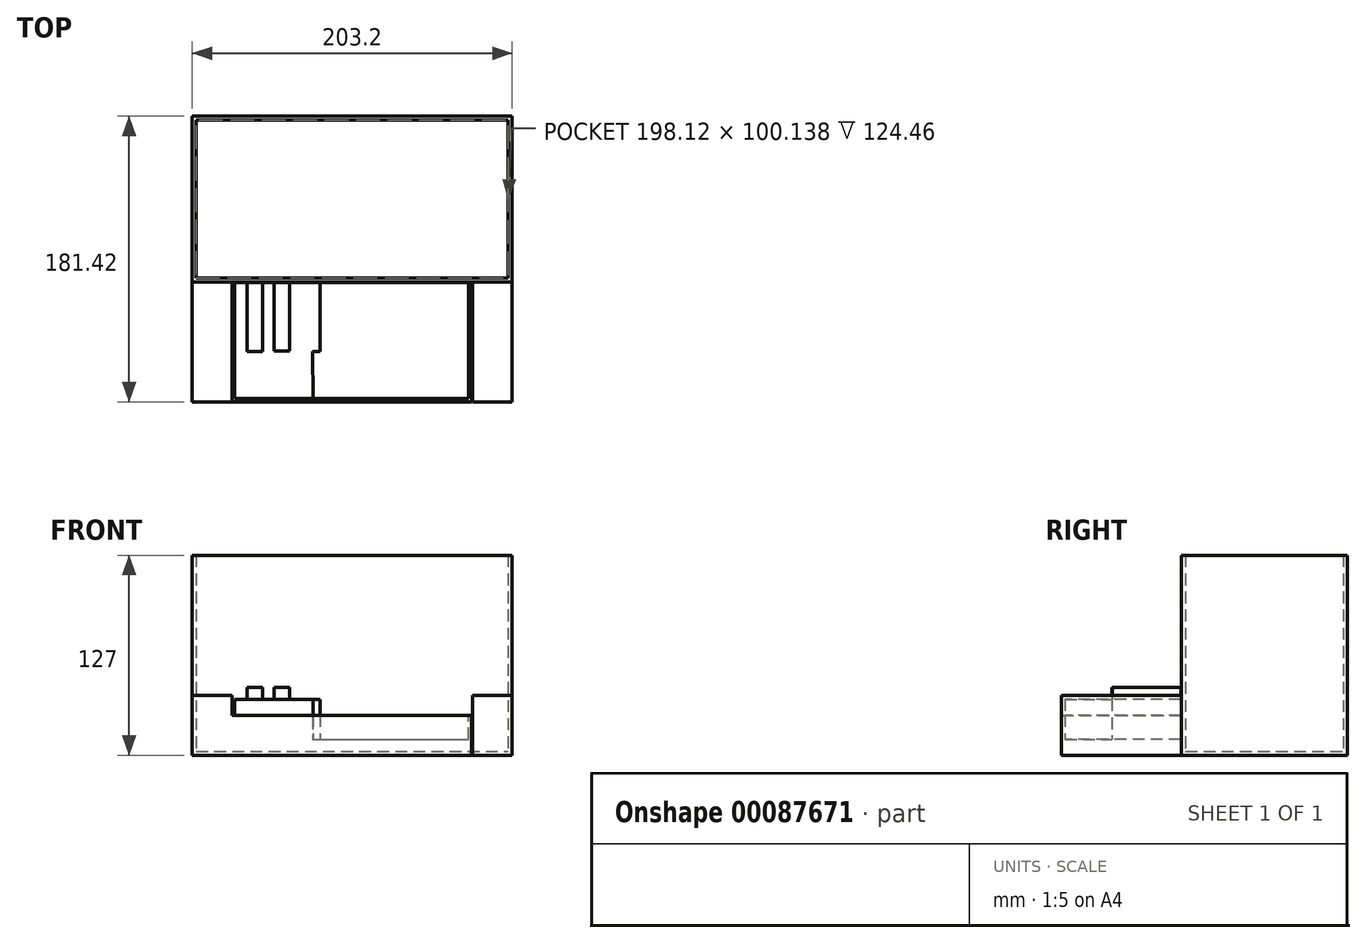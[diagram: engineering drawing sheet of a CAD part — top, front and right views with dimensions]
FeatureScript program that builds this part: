
annotation { "Feature Type Name" : "Feature", "Feature Type Description" : "" }
export const myFeature = defineFeature(function(context is Context, id is Id, definition is map)
    precondition{}
    {
        {
            var Q0;
            Q0=qCreatedBy(makeId("Top.planeOp"),FACE);
            var sketch = newSketch(context, id + "F0", { "sketchPlane" : qUnion([Q0])});
            skLineSegment(sketch, "E0.bottom", {"start": v(-102.58, 0) * mm, "end": v(100.62, 0) * mm});
            skLineSegment(sketch, "E0.top", {"start": v(-102.58, 105.22) * mm, "end": v(100.62, 105.22) * mm});
            skLineSegment(sketch, "E0.left", {"start": v(-102.58, 0) * mm, "end": v(-102.58, 105.22) * mm});
            skLineSegment(sketch, "E0.right", {"start": v(100.62, 0) * mm, "end": v(100.62, 105.22) * mm});
            skSolve(sketch);
        }
        {
            var Q0;
            Q0=makeQuery(id+"F0.imprint","IMPRINT",FACE,{"disambiguationData":[TD([[makeQuery(id+"F0.imprint","IMPRINT",EDGE,{"derivedFrom":sQuery(id+"F0.wireOp",EDGE,"E0.bottom")}),1.0]])]});
            extrude(context, id + "F1", {"entities" : qUnion([Q0]), "depth" : 127 * mm});
        }
        {
            var Q0;
            Q0=makeQuery(id+"F1.opExtrude","CAP_FACE",FACE,{"disambiguationData":[OSD([sQuery(id+"F0.wireOp",EDGE,"E0.bottom"),sQuery(id+"F0.wireOp",EDGE,"E0.top"),sQuery(id+"F0.wireOp",EDGE,"E0.left"),sQuery(id+"F0.wireOp",EDGE,"E0.right")])],"isStart":false});
            shell(context, id + "F2", {"entities" : qUnion([Q0]), "thickness" : 2.54 * mm});
        }
        {
            var Q0;
            Q0=makeQuery(id+"F1.opExtrude","SWEPT_FACE",FACE,{"disambiguationData":[OSD([sQuery(id+"F0.wireOp",EDGE,"E0.bottom")])]});
            var sketch = newSketch(context, id + "F3", { "sketchPlane" : qUnion([Q0])});
            skLineSegment(sketch, "E1.bottom", {"start": v(-77.18, 86.09) * mm, "end": v(75.22, 86.09) * mm});
            skLineSegment(sketch, "E1.top", {"start": v(-77.18, 25.4) * mm, "end": v(75.22, 25.4) * mm});
            skLineSegment(sketch, "E1.left", {"start": v(-77.18, 86.09) * mm, "end": v(-77.18, 25.4) * mm});
            skLineSegment(sketch, "E1.right", {"start": v(75.22, 86.09) * mm, "end": v(75.22, 25.4) * mm});
            skSolve(sketch);
        }
        {
            var Q0;
            Q0=makeQuery(id+"F3.imprint","IMPRINT",FACE,{"disambiguationData":[TD([[makeQuery(id+"F3.imprint","IMPRINT",EDGE,{"derivedFrom":sQuery(id+"F3.wireOp",EDGE,"E1.bottom")}),1.0]])]});
            var sketch = newSketch(context, id + "F4", { "sketchPlane" : qUnion([Q0])});
            skLineSegment(sketch, "E2.bottom", {"start": v(-77.05, 26.02) * mm, "end": v(75, 26.02) * mm});
            skLineSegment(sketch, "E2.top", {"start": v(-77.05, 0) * mm, "end": v(75, 0) * mm});
            skLineSegment(sketch, "E2.left", {"start": v(-77.05, 26.02) * mm, "end": v(-77.05, 0) * mm});
            skLineSegment(sketch, "E2.right", {"start": v(75, 26.02) * mm, "end": v(75, 0) * mm});
            skLineSegment(sketch, "E3.bottom", {"start": v(75.56, 37.95) * mm, "end": v(100.55, 37.95) * mm});
            skLineSegment(sketch, "E3.top", {"start": v(75.56, 0) * mm, "end": v(100.55, 0) * mm});
            skLineSegment(sketch, "E3.left", {"start": v(75.56, 37.95) * mm, "end": v(75.56, 0) * mm});
            skLineSegment(sketch, "E3.right", {"start": v(100.55, 37.95) * mm, "end": v(100.55, 0) * mm});
            skLineSegment(sketch, "E4.bottom", {"start": v(-76.22, 37.95) * mm, "end": v(-102.53, 37.95) * mm});
            skLineSegment(sketch, "E4.top", {"start": v(-76.22, 0) * mm, "end": v(-102.53, 0) * mm});
            skLineSegment(sketch, "E4.left", {"start": v(-76.22, 37.95) * mm, "end": v(-76.22, 0) * mm});
            skLineSegment(sketch, "E4.right", {"start": v(-102.53, 37.95) * mm, "end": v(-102.53, 0) * mm});
            skSolve(sketch);
        }
        {
            var Q0;
            {var subQ0=sQuery(id+"F4.wireOp",EDGE,"E4.right");Q0=makeQuery(id+"F4.imprint","IMPRINT",FACE,{"disambiguationData":[TD([[makeQuery(id+"F4.imprint","IMPRINT",EDGE,{"derivedFrom":subQ0}),1.0]])]});}
            var Q1;
            Q1=makeQuery(id+"F4.imprint","IMPRINT",FACE,{"disambiguationData":[TD([[makeQuery(id+"F4.imprint","IMPRINT",EDGE,{"derivedFrom":sQuery(id+"F4.wireOp",EDGE,"E3.bottom")}),-1.0]])]});
            var Q2;
            {var subQ0=sQuery(id+"F4.wireOp",EDGE,"E2.top");Q2=makeQuery(id+"F4.imprint","IMPRINT",FACE,{"disambiguationData":[TD([[makeQuery(id+"F4.imprint","IMPRINT",EDGE,{"derivedFrom":subQ0}),1.0]])]});}
            extrude(context, id + "F5", {"entities" : qUnion([Q0, Q1, Q2]), "operationType" : NewBodyOperationType.ADD, "depth" : 76.2 * mm});
        }
        {
            var Q0;
            {var subQ0=sQuery(id+"F3.wireOp",EDGE,"E1.top");var subQ1=makeQuery(id+"F3.imprint","IMPRINT",EDGE,{"derivedFrom":subQ0});Q0=makeQuery(id+"F5.opExtrude","SWEPT_FACE",FACE,{"disambiguationData":[OSD([subQ0]),TDD([makeQuery(id+"F4.imprint","IMPRINT",EDGE,{"disambiguationData":[TD([[makeQuery(id+"F4.imprint","INTERSECT",VERTEX,{"derivedFrom":[subQ1,sQuery(id+"F4.wireOp",EDGE,"E2.right")]}),1.0]])],"derivedFrom":subQ1})])]});}
            var sketch = newSketch(context, id + "F6", { "sketchPlane" : qUnion([Q0])});
            skLineSegment(sketch, "E5.bottom", {"start": v(-75.7, -0.56) * mm, "end": v(73.11, -0.56) * mm});
            skLineSegment(sketch, "E5.top", {"start": v(-75.7, -74) * mm, "end": v(73.11, -74) * mm});
            skLineSegment(sketch, "E5.left", {"start": v(-75.7, -0.56) * mm, "end": v(-75.7, -74) * mm});
            skLineSegment(sketch, "E5.right", {"start": v(73.11, -0.56) * mm, "end": v(73.11, -74) * mm});
            skSolve(sketch);
        }
        {
            var Q0;
            Q0=makeQuery(id+"F6.imprint","IMPRINT",FACE,{"disambiguationData":[TD([[makeQuery(id+"F6.imprint","IMPRINT",EDGE,{"derivedFrom":sQuery(id+"F6.wireOp",EDGE,"E5.bottom")}),-1.0]])]});
            extrude(context, id + "F7", {"entities" : qUnion([Q0]), "operationType" : NewBodyOperationType.REMOVE, "oppositeDirection" : true, "depth" : 15.24 * mm});
        }
        {
            var Q0;
            Q0=makeQuery(id+"F7.boolean.opBoolean","COPY",FACE,{"derivedFrom":makeQuery(id+"F7.opExtrude","CAP_FACE",FACE,{"disambiguationData":[OSD([sQuery(id+"F6.wireOp",EDGE,"E5.bottom"),sQuery(id+"F6.wireOp",EDGE,"E5.top"),sQuery(id+"F6.wireOp",EDGE,"E5.left"),sQuery(id+"F6.wireOp",EDGE,"E5.right")])],"isStart":false})});
            var sketch = newSketch(context, id + "F8", { "sketchPlane" : qUnion([Q0])});
            skLineSegment(sketch, "E6.bottom", {"start": v(-67.63, -0.56) * mm, "end": v(-57.73, -0.56) * mm});
            skLineSegment(sketch, "E6.top", {"start": v(-67.63, -44.15) * mm, "end": v(-57.73, -44.15) * mm});
            skLineSegment(sketch, "E6.left", {"start": v(-67.63, -0.56) * mm, "end": v(-67.63, -44.15) * mm});
            skLineSegment(sketch, "E6.right", {"start": v(-57.73, -0.56) * mm, "end": v(-57.73, -44.15) * mm});
            skLineSegment(sketch, "E7.bottom", {"start": v(-50.45, -0.56) * mm, "end": v(-40.86, -0.56) * mm});
            skLineSegment(sketch, "E7.top", {"start": v(-50.45, -44.07) * mm, "end": v(-40.86, -44.07) * mm});
            skLineSegment(sketch, "E7.left", {"start": v(-50.45, -0.56) * mm, "end": v(-50.45, -44.07) * mm});
            skLineSegment(sketch, "E7.right", {"start": v(-40.86, -0.56) * mm, "end": v(-40.86, -44.07) * mm});
            skLineSegment(sketch, "E8", {"start": v(-48.25, -44.07) * mm, "end": v(-48.25, -74) * mm});
            skLineSegment(sketch, "E9", {"start": v(-59.98, -44.15) * mm, "end": v(-59.98, -74) * mm});
            skLineSegment(sketch, "E10", {"start": v(-59.98, -74) * mm, "end": v(-75.7, -74) * mm});
            skLineSegment(sketch, "E11", {"start": v(-75.7, -74) * mm, "end": v(-59.98, -74) * mm});
            skLineSegment(sketch, "E12.bottom", {"start": v(-75.7, -0.56) * mm, "end": v(-59.98, -0.56) * mm});
            skLineSegment(sketch, "E12.left", {"start": v(-75.7, -0.56) * mm, "end": v(-75.7, -74) * mm});
            skLineSegment(sketch, "E13", {"start": v(-59.98, -74) * mm, "end": v(-48.25, -74) * mm});
            skLineSegment(sketch, "E14", {"start": v(-36.07, -0.56) * mm, "end": v(-36.07, -74) * mm});
            skLineSegment(sketch, "E15.bottom", {"start": v(-36.07, -0.56) * mm, "end": v(-25.77, -0.56) * mm});
            skLineSegment(sketch, "E15.top", {"start": v(-36.07, -74) * mm, "end": v(-25.77, -74) * mm});
            skLineSegment(sketch, "E16.bottom", {"start": v(-30.92, -0.56) * mm, "end": v(-21.45, -0.56) * mm});
            skLineSegment(sketch, "E16.top", {"start": v(-30.92, -44.3) * mm, "end": v(-21.45, -44.3) * mm});
            skLineSegment(sketch, "E16.left", {"start": v(-30.92, -0.56) * mm, "end": v(-30.92, -44.3) * mm});
            skLineSegment(sketch, "E16.right", {"start": v(-21.45, -0.56) * mm, "end": v(-21.45, -44.3) * mm});
            skLineSegment(sketch, "E17.bottom", {"start": v(-26.9, -76.69) * mm, "end": v(-23.81, -76.69) * mm});
            skLineSegment(sketch, "E17.top", {"start": v(-26.9, -83.44) * mm, "end": v(-23.81, -83.44) * mm});
            skLineSegment(sketch, "E17.left", {"start": v(-26.9, -76.69) * mm, "end": v(-26.9, -83.44) * mm});
            skLineSegment(sketch, "E17.right", {"start": v(-23.81, -76.69) * mm, "end": v(-23.81, -83.44) * mm});
            skLineSegment(sketch, "E18", {"start": v(-25.77, -74) * mm, "end": v(-26.18, -44.3) * mm});
            skSolve(sketch);
        }
        {
            var Q0;
            {var subQ1=sQuery(id+"F8.wireOp",EDGE,"E6.right");Q0=makeQuery(id+"F8.imprint","IMPRINT",FACE,{"disambiguationData":[TD([[makeQuery(id+"F8.imprint","IMPRINT",EDGE,{"derivedFrom":subQ1}),1.0]])]});}
            var Q1;
            {var subQ2=sQuery(id+"F8.wireOp",EDGE,"E6.left");Q1=makeQuery(id+"F8.imprint","IMPRINT",FACE,{"disambiguationData":[TD([[makeQuery(id+"F8.imprint","IMPRINT",EDGE,{"derivedFrom":subQ2}),-1.0]])]});}
            var Q2;
            Q2=makeQuery(id+"F8.imprint","IMPRINT",FACE,{"disambiguationData":[TD([[makeQuery(id+"F8.imprint","IMPRINT",EDGE,{"derivedFrom":sQuery(id+"F8.wireOp",EDGE,"E15.bottom")}),-1.0]])]});
            var Q3;
            {var subQ2=sQuery(id+"F8.wireOp",EDGE,"E7.right");Q3=makeQuery(id+"F8.imprint","IMPRINT",FACE,{"disambiguationData":[TD([[makeQuery(id+"F8.imprint","IMPRINT",EDGE,{"derivedFrom":subQ2}),1.0]])]});}
            extrude(context, id + "F9", {"entities" : qUnion([Q0, Q1, Q2, Q3]), "operationType" : NewBodyOperationType.ADD, "depth" : 25.4 * mm});
        }
        {
            var Q0;
            {var subQ0=sQuery(id+"F6.wireOp",EDGE,"E5.bottom");Q0=makeQuery(id+"F9.boolean.opBoolean","SPLIT",FACE,{"disambiguationData":[TD([makeQuery(id+"F9.opExtrude","SWEPT_FACE",FACE,{"disambiguationData":[OSD([sQuery(id+"F8.wireOp",EDGE,"E6.top")])]})])],"derivedFrom":makeQuery(id+"F7.boolean.opBoolean","COPY",FACE,{"derivedFrom":makeQuery(id+"F7.opExtrude","CAP_FACE",FACE,{"disambiguationData":[OSD([subQ0,sQuery(id+"F6.wireOp",EDGE,"E5.top"),sQuery(id+"F6.wireOp",EDGE,"E5.left"),sQuery(id+"F6.wireOp",EDGE,"E5.right")])],"isStart":false})})});}
            var Q1;
            {var subQ0=sQuery(id+"F6.wireOp",EDGE,"E5.bottom");Q1=makeQuery(id+"F9.boolean.opBoolean","SPLIT",FACE,{"disambiguationData":[TD([makeQuery(id+"F9.opExtrude","SWEPT_FACE",FACE,{"disambiguationData":[OSD([sQuery(id+"F8.wireOp",EDGE,"E7.top")])]})])],"derivedFrom":makeQuery(id+"F7.boolean.opBoolean","COPY",FACE,{"derivedFrom":makeQuery(id+"F7.opExtrude","CAP_FACE",FACE,{"disambiguationData":[OSD([subQ0,sQuery(id+"F6.wireOp",EDGE,"E5.top"),sQuery(id+"F6.wireOp",EDGE,"E5.left"),sQuery(id+"F6.wireOp",EDGE,"E5.right")])],"isStart":false})})});}
            extrude(context, id + "F10", {"entities" : qUnion([Q0, Q1]), "operationType" : NewBodyOperationType.ADD, "depth" : 33.02 * mm});
        }
    });
